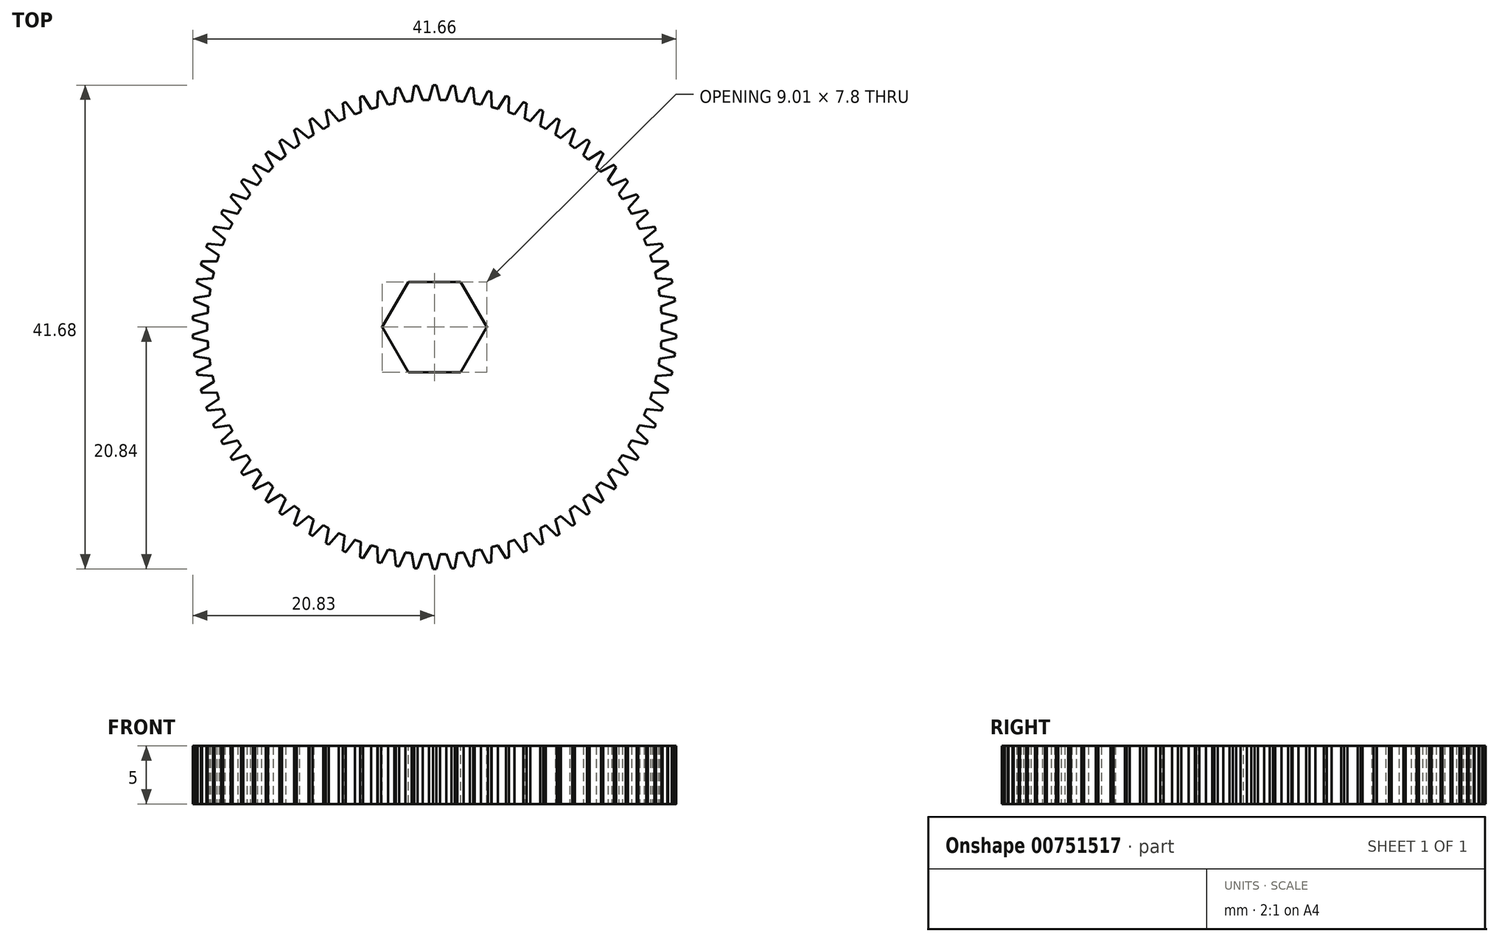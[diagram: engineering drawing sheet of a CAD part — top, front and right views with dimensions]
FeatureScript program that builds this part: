
annotation { "Feature Type Name" : "Feature", "Feature Type Description" : "" }
export const myFeature = defineFeature(function(context is Context, id is Id, definition is map)
    precondition{}
    {
        {
            assignVariable(context, id + "F0", {"name" : "GearHeight", "anyValue" : 5 * mm});
        }
        {
            assignVariable(context, id + "F1", {"name" : "teeth", "anyValue" : 82});
        }
        {
            var Q0;
            Q0=qCreatedBy(makeId("Top.planeOp"),FACE);
            var sketch = newSketch(context, id + "F2", { "sketchPlane" : qUnion([Q0])});
            skCircle(sketch, "E0", {"center": v(0, 0) * mm, "radius": 19.59 * mm});
            skCircle(sketch, "E1", {"center": v(0, 0) * mm, "radius": 20.84 * mm});
            skLineSegment(sketch, "E2", {"start": v(0.48, 19.58) * mm, "end": v(0.14, 20.84) * mm});
            skLineSegment(sketch, "E3", {"start": v(-0.48, 19.58) * mm, "end": v(-0.14, 20.84) * mm});
            skLineSegment(sketch, "E4", {"start": v(0, 0) * mm, "end": v(0, 64.06) * mm, "construction": true});
            skArc(sketch, "E5", {"start": v(-0.48, 19.58) * mm, "mid": v(-0.24, 19.58) * mm, "end": v(0, 19.59) * mm});
            skArc(sketch, "E6", {"start": v(0.48, 19.58) * mm, "mid": v(0.24, 19.58) * mm, "end": v(0, 19.59) * mm});
            skCircle(sketch, "E7", {"center": v(0, 0) * mm, "radius": 20.21 * mm, "construction": true});
            skPoint(sketch, "E8", {"position": v(-0.31, 20.2) * mm});
            skArc(sketch, "E9", {"start": v(0.14, 20.84) * mm, "mid": v(0.07, 20.84) * mm, "end": v(0, 20.84) * mm});
            skArc(sketch, "E10", {"start": v(-0.14, 20.84) * mm, "mid": v(-0.07, 20.84) * mm, "end": v(0, 20.84) * mm});
            skPoint(sketch, "E11", {"position": v(0.31, 20.2) * mm});
            skSolve(sketch);
        }
        {
            var Q0;
            Q0=qCreatedBy(makeId("Right.planeOp"),FACE);
            var sketch = newSketch(context, id + "F3", { "sketchPlane" : qUnion([Q0])});
            skLineSegment(sketch, "E12", {"start": v(0, 16.96) * mm, "end": v(0, -9.96) * mm, "construction": true});
            skSolve(sketch);
        }
        {
            var Q0;
            {var subQ0=sQuery(id+"F2.wireOp",EDGE,"E0");var subQ1=makeQuery(id+"F2.imprint","INTERSECT",VERTEX,{"derivedFrom":[subQ0,sQuery(id+"F2.wireOp",EDGE,"E2")]});Q0=makeQuery(id+"F2.imprint","IMPRINT",FACE,{"disambiguationData":[TD([[makeQuery(id+"F2.imprint","IMPRINT",EDGE,{"disambiguationData":[TD([[subQ1,-1.0]])],"derivedFrom":subQ0}),1.0]])]});}
            extrude(context, id + "F4", {"entities" : qUnion([Q0]), "depth" : getVariable(context, 'GearHeight'), "offsetDistance" : 25 * mm});
        }
        {
            var Q0;
            {var subQ0=sQuery(id+"F2.wireOp",EDGE,"E2");Q0=makeQuery(id+"F2.imprint","IMPRINT",FACE,{"disambiguationData":[TD([[makeQuery(id+"F2.imprint","IMPRINT",EDGE,{"derivedFrom":subQ0}),1.0]])]});}
            extrude(context, id + "F5", {"entities" : qUnion([Q0]), "operationType" : NewBodyOperationType.ADD, "depth" : getVariable(context, 'GearHeight'), "offsetDistance" : 25 * mm});
        }
        {
            var Q0;
            Q0=makeQuery(id+"F4.opExtrude","SWEPT_BODY",BODY,{"disambiguationData":[OSD([sQuery(id+"F2.wireOp",EDGE,"E0")])]});
            var Q1;
            Q1=sQuery(id+"F3.wireOp",EDGE,"E12");
            circularPattern(context, id + "F6", {"operationType" : NewBodyOperationType.ADD, "entities" : qUnion([Q0]), "axis" : qUnion([Q1]), "angle" : 360 * degree, "instanceCount" : getVariable(context, 'teeth'), "equalSpace" : true});
        }
        {
            var Q0;
            {var subQ0=sQuery(id+"F2.wireOp",EDGE,"E0");var subQ1=makeQuery(id+"F5.boolean.opBoolean","MERGE",FACE,{"derivedFrom":[makeQuery(id+"F4.opExtrude","CAP_FACE",FACE,{"disambiguationData":[OSD([subQ0])],"isStart":false}),makeQuery(id+"F5.opExtrude","CAP_FACE",FACE,{"disambiguationData":[OSD([subQ0,sQuery(id+"F2.wireOp",EDGE,"E1"),sQuery(id+"F2.wireOp",EDGE,"E2"),sQuery(id+"F2.wireOp",EDGE,"E3")])],"isStart":false})]});Q0=makeQuery(id+"F6.boolean.opBoolean","MERGE",FACE,{"derivedFrom":[subQ1,makeQuery(id+"F6.opPattern","COPY",FACE,{"derivedFrom":subQ1,"instanceName":"1"}),makeQuery(id+"F6.opPattern","COPY",FACE,{"derivedFrom":subQ1,"instanceName":"2"}),makeQuery(id+"F6.opPattern","COPY",FACE,{"derivedFrom":subQ1,"instanceName":"3"}),makeQuery(id+"F6.opPattern","COPY",FACE,{"derivedFrom":subQ1,"instanceName":"4"}),makeQuery(id+"F6.opPattern","COPY",FACE,{"derivedFrom":subQ1,"instanceName":"5"}),makeQuery(id+"F6.opPattern","COPY",FACE,{"derivedFrom":subQ1,"instanceName":"6"}),makeQuery(id+"F6.opPattern","COPY",FACE,{"derivedFrom":subQ1,"instanceName":"7"}),makeQuery(id+"F6.opPattern","COPY",FACE,{"derivedFrom":subQ1,"instanceName":"8"}),makeQuery(id+"F6.opPattern","COPY",FACE,{"derivedFrom":subQ1,"instanceName":"9"}),makeQuery(id+"F6.opPattern","COPY",FACE,{"derivedFrom":subQ1,"instanceName":"10"}),makeQuery(id+"F6.opPattern","COPY",FACE,{"derivedFrom":subQ1,"instanceName":"11"}),makeQuery(id+"F6.opPattern","COPY",FACE,{"derivedFrom":subQ1,"instanceName":"12"}),makeQuery(id+"F6.opPattern","COPY",FACE,{"derivedFrom":subQ1,"instanceName":"13"}),makeQuery(id+"F6.opPattern","COPY",FACE,{"derivedFrom":subQ1,"instanceName":"14"}),makeQuery(id+"F6.opPattern","COPY",FACE,{"derivedFrom":subQ1,"instanceName":"15"}),makeQuery(id+"F6.opPattern","COPY",FACE,{"derivedFrom":subQ1,"instanceName":"16"}),makeQuery(id+"F6.opPattern","COPY",FACE,{"derivedFrom":subQ1,"instanceName":"17"}),makeQuery(id+"F6.opPattern","COPY",FACE,{"derivedFrom":subQ1,"instanceName":"18"}),makeQuery(id+"F6.opPattern","COPY",FACE,{"derivedFrom":subQ1,"instanceName":"19"}),makeQuery(id+"F6.opPattern","COPY",FACE,{"derivedFrom":subQ1,"instanceName":"20"}),makeQuery(id+"F6.opPattern","COPY",FACE,{"derivedFrom":subQ1,"instanceName":"21"}),makeQuery(id+"F6.opPattern","COPY",FACE,{"derivedFrom":subQ1,"instanceName":"22"}),makeQuery(id+"F6.opPattern","COPY",FACE,{"derivedFrom":subQ1,"instanceName":"23"}),makeQuery(id+"F6.opPattern","COPY",FACE,{"derivedFrom":subQ1,"instanceName":"24"})]});}
            var sketch = newSketch(context, id + "F7", { "sketchPlane" : qUnion([Q0])});
            skCircle(sketch, "E13.cCircle", {"center": v(0, 0) * mm, "radius": 3.9 * mm, "construction": true});
            skLineSegment(sketch, "E13.0", {"start": v(-2.25, 3.9) * mm, "end": v(2.25, 3.9) * mm});
            skLineSegment(sketch, "E13.1", {"start": v(2.25, 3.9) * mm, "end": v(4.5, 0) * mm});
            skLineSegment(sketch, "E13.2", {"start": v(4.5, 0) * mm, "end": v(2.25, -3.9) * mm});
            skLineSegment(sketch, "E13.3", {"start": v(2.25, -3.9) * mm, "end": v(-2.25, -3.9) * mm});
            skLineSegment(sketch, "E13.4", {"start": v(-2.25, -3.9) * mm, "end": v(-4.5, 0) * mm});
            skLineSegment(sketch, "E13.5", {"start": v(-4.5, 0) * mm, "end": v(-2.25, 3.9) * mm});
            skPoint(sketch, "E13.0.midPoint", {"position": v(0, 3.9) * mm});
            skSolve(sketch);
        }
        {
            var Q0;
            Q0=makeQuery(id+"F7.imprint","IMPRINT",FACE,{"disambiguationData":[TD([[makeQuery(id+"F7.imprint","IMPRINT",EDGE,{"derivedFrom":sQuery(id+"F7.wireOp",EDGE,"E13.0")}),-1.0]])]});
            extrude(context, id + "F8", {"entities" : qUnion([Q0]), "operationType" : NewBodyOperationType.REMOVE, "endBound" : BoundingType.THROUGH_ALL, "oppositeDirection" : true, "depth" : 25 * mm, "offsetDistance" : 25 * mm});
        }
    });
